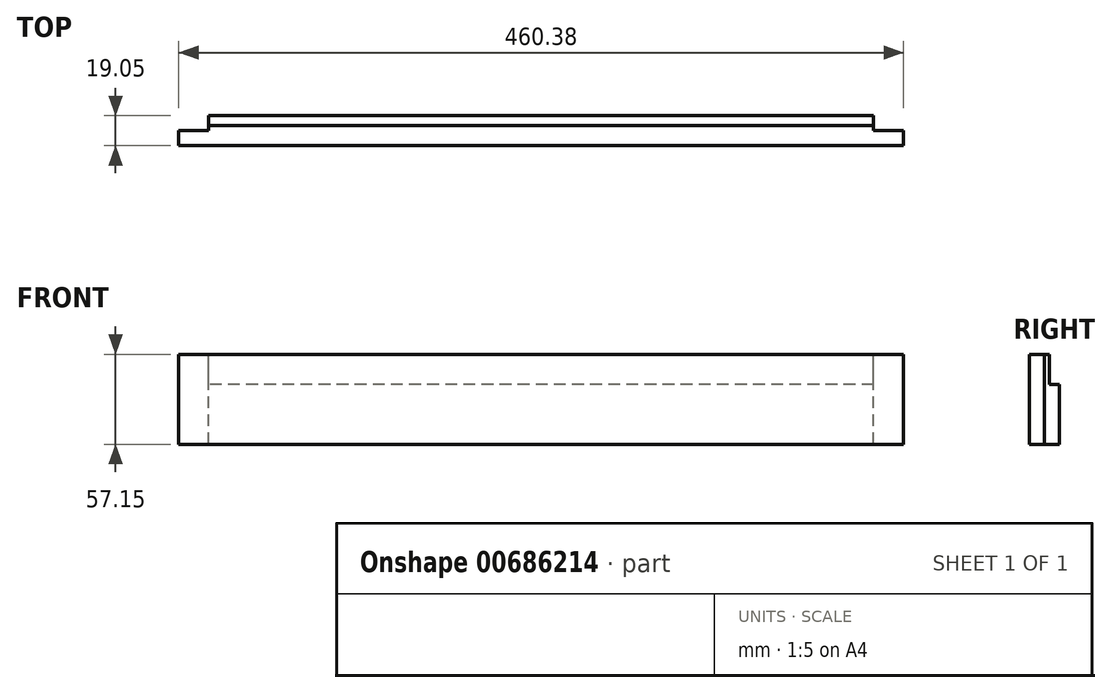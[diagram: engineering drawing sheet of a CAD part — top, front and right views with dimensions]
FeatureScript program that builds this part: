
annotation { "Feature Type Name" : "Feature", "Feature Type Description" : "" }
export const myFeature = defineFeature(function(context is Context, id is Id, definition is map)
    precondition{}
    {
        {
            var Q0;
            Q0=qCreatedBy(makeId("Right.planeOp"),FACE);
            var sketch = newSketch(context, id + "F0", { "sketchPlane" : qUnion([Q0])});
            skLineSegment(sketch, "E0.top", {"start": v(-19.05, 0) * mm, "end": v(0, 0) * mm});
            skLineSegment(sketch, "E0.left", {"start": v(-19.05, 57.15) * mm, "end": v(-19.05, 0) * mm});
            skLineSegment(sketch, "E0.right", {"start": v(0, 38.1) * mm, "end": v(0, 0) * mm});
            skLineSegment(sketch, "E1", {"start": v(-6.35, 57.15) * mm, "end": v(-6.35, 38.1) * mm});
            skLineSegment(sketch, "E2", {"start": v(-6.35, 38.1) * mm, "end": v(0, 38.1) * mm});
            skLineSegment(sketch, "E3", {"start": v(-19.05, 57.15) * mm, "end": v(-6.35, 57.15) * mm});
            skSolve(sketch);
        }
        {
            var Q0;
            Q0 = qSketchRegion(id + "F0", true);
            extrude(context, id + "F1", {"entities" : qUnion([Q0]), "endBound" : BoundingType.SYMMETRIC, "depth" : 460.38 * mm, "offsetDistance" : 25.4 * mm});
        }
        {
            var Q0;
            Q0=qCreatedBy(makeId("Top.planeOp"),FACE);
            var sketch = newSketch(context, id + "F2", { "sketchPlane" : qUnion([Q0])});
            skLineSegment(sketch, "E4.bottom", {"start": v(230.19, 0) * mm, "end": v(211.14, 0) * mm});
            skLineSegment(sketch, "E4.top", {"start": v(230.19, -9.53) * mm, "end": v(211.14, -9.53) * mm});
            skLineSegment(sketch, "E4.left", {"start": v(230.19, 0) * mm, "end": v(230.19, -9.53) * mm});
            skLineSegment(sketch, "E4.right", {"start": v(211.14, 0) * mm, "end": v(211.14, -9.53) * mm});
            skLineSegment(sketch, "E5", {"start": v(0, 0) * mm, "end": v(0, -304.9) * mm, "construction": true});
            skLineSegment(sketch, "E6.MirrorCS", {"start": v(-211.14, 0) * mm, "end": v(-211.14, -9.53) * mm});
            skLineSegment(sketch, "E7.MirrorCS", {"start": v(-230.19, 0) * mm, "end": v(-230.19, -9.53) * mm});
            skLineSegment(sketch, "E8.MirrorCS", {"start": v(-230.19, -9.53) * mm, "end": v(-211.14, -9.53) * mm});
            skLineSegment(sketch, "E9.MirrorCS", {"start": v(-230.19, 0) * mm, "end": v(-211.14, 0) * mm});
            skSolve(sketch);
        }
        {
            var Q0;
            Q0 = qSketchRegion(id + "F2", true);
            extrude(context, id + "F3", {"entities" : qUnion([Q0]), "operationType" : NewBodyOperationType.REMOVE, "endBound" : BoundingType.THROUGH_ALL, "oppositeDirection" : true, "depth" : 25.4 * mm, "offsetDistance" : 25.4 * mm, "hasSecondDirection" : true, "secondDirectionBound" : SecondDirectionBoundingType.THROUGH_ALL, "secondDirectionOppositeDirection" : false, "secondDirectionDepth" : 25.4 * mm});
        }
    });
